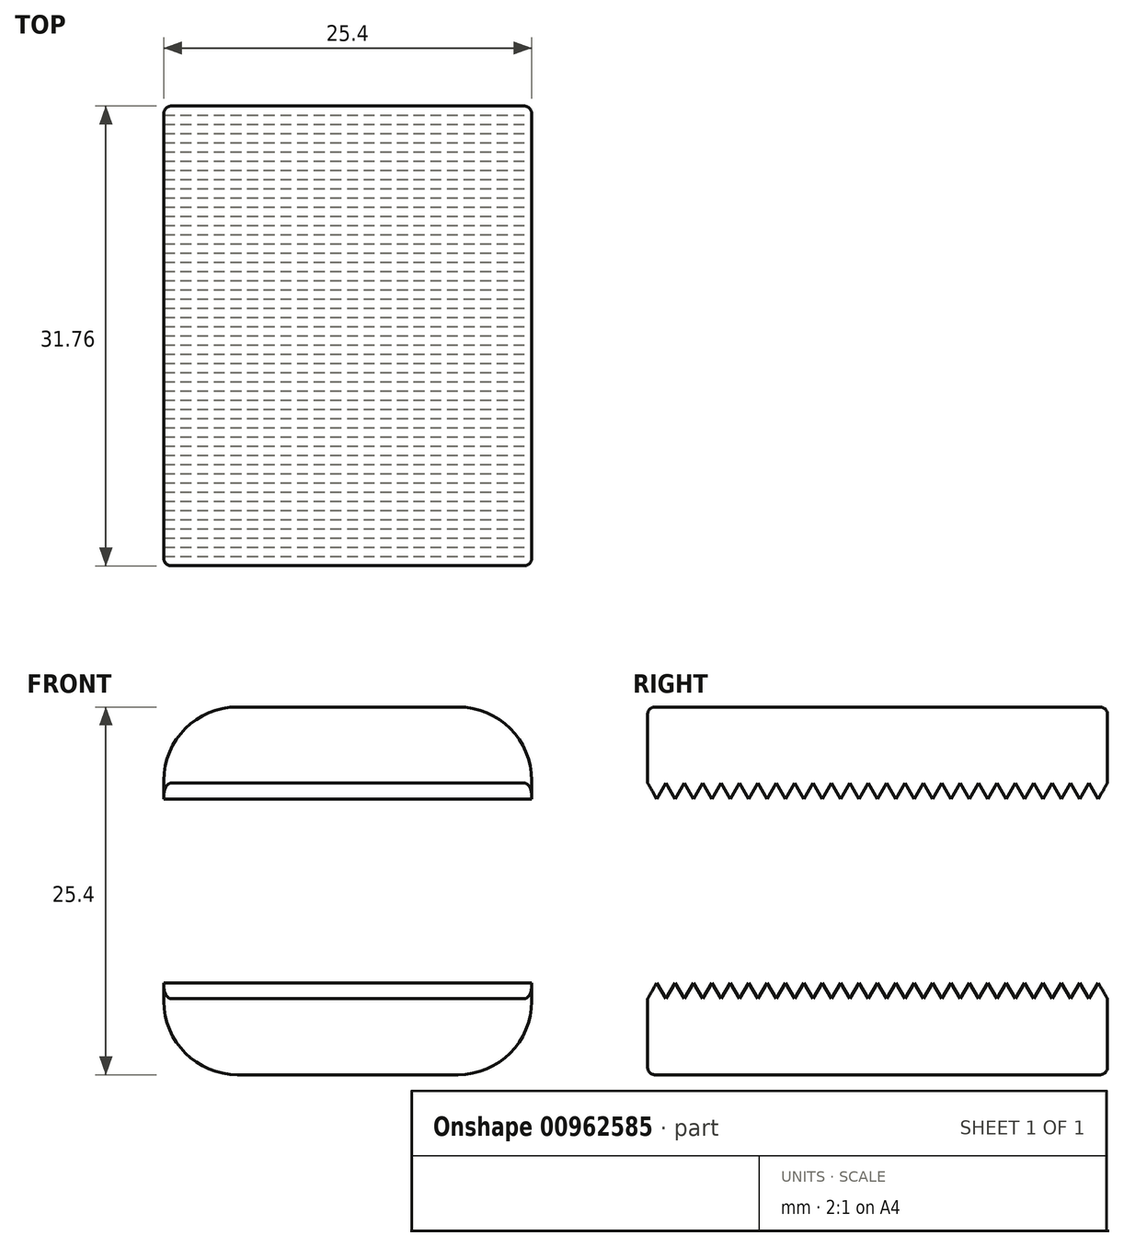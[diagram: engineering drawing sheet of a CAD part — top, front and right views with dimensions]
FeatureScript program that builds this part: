
annotation { "Feature Type Name" : "Feature", "Feature Type Description" : "" }
export const myFeature = defineFeature(function(context is Context, id is Id, definition is map)
    precondition{}
    {
        {
            var Q0;
            Q0=qCreatedBy(makeId("Front.planeOp"),FACE);
            var sketch = newSketch(context, id + "F0", { "sketchPlane" : qUnion([Q0])});
            skLineSegment(sketch, "E0.bottom", {"start": v(12.7, -12.7) * mm, "end": v(-12.7, -12.7) * mm});
            skLineSegment(sketch, "E0.top", {"start": v(12.7, 12.7) * mm, "end": v(-12.7, 12.7) * mm});
            skLineSegment(sketch, "E0.left", {"start": v(12.7, -12.7) * mm, "end": v(12.7, -6.35) * mm});
            skLineSegment(sketch, "E0.right", {"start": v(-12.7, -12.7) * mm, "end": v(-12.7, -6.35) * mm});
            skPoint(sketch, "E0.middle", {"position": v(0, 0) * mm});
            skLineSegment(sketch, "E1.bottom", {"start": v(12.7, -6.35) * mm, "end": v(-12.7, -6.35) * mm});
            skLineSegment(sketch, "E1.top", {"start": v(12.7, 6.35) * mm, "end": v(-12.7, 6.35) * mm});
            skLineSegment(sketch, "E2.trimOffspring", {"start": v(-12.7, 6.35) * mm, "end": v(-12.7, 12.7) * mm});
            skLineSegment(sketch, "E3.trimOffspring", {"start": v(12.7, 6.35) * mm, "end": v(12.7, 12.7) * mm});
            skSolve(sketch);
        }
        {
            var Q0;
            Q0=qSketchRegion(id+"F0",true);
            extrude(context, id + "F1", {"entities" : qUnion([Q0]), "endBound" : BoundingType.SYMMETRIC, "depth" : 31.75 * mm, "offsetDistance" : 25.4 * mm});
        }
        {
            var Q0;
            Q0=qCreatedBy(makeId("Right.planeOp"),FACE);
            var sketch = newSketch(context, id + "F2", { "sketchPlane" : qUnion([Q0])});
            skLineSegment(sketch, "E4", {"start": v(0, 6.35) * mm, "end": v(-0.64, 7.45) * mm});
            skLineSegment(sketch, "E5", {"start": v(-0.63, 7.45) * mm, "end": v(-1.27, 6.35) * mm});
            skLineSegment(sketch, "E6.1.0.0", {"start": v(-1.27, 6.35) * mm, "end": v(-1.9, 7.45) * mm});
            skLineSegment(sketch, "E6.1.0.1", {"start": v(-1.9, 7.45) * mm, "end": v(-2.54, 6.35) * mm});
            skLineSegment(sketch, "E6.2.0.0", {"start": v(-2.54, 6.35) * mm, "end": v(-3.18, 7.45) * mm});
            skLineSegment(sketch, "E6.2.0.1", {"start": v(-3.18, 7.45) * mm, "end": v(-3.81, 6.35) * mm});
            skLineSegment(sketch, "E6.3.0.0", {"start": v(-3.81, 6.35) * mm, "end": v(-4.45, 7.45) * mm});
            skLineSegment(sketch, "E6.3.0.1", {"start": v(-4.45, 7.45) * mm, "end": v(-5.08, 6.35) * mm});
            skLineSegment(sketch, "E6.4.0.0", {"start": v(-5.08, 6.35) * mm, "end": v(-5.72, 7.45) * mm});
            skLineSegment(sketch, "E6.4.0.1", {"start": v(-5.72, 7.45) * mm, "end": v(-6.35, 6.35) * mm});
            skLineSegment(sketch, "E6.5.0.0", {"start": v(-6.35, 6.35) * mm, "end": v(-6.99, 7.45) * mm});
            skLineSegment(sketch, "E6.5.0.1", {"start": v(-6.99, 7.45) * mm, "end": v(-7.62, 6.35) * mm});
            skLineSegment(sketch, "E6.6.0.0", {"start": v(-7.62, 6.35) * mm, "end": v(-8.26, 7.45) * mm});
            skLineSegment(sketch, "E6.6.0.1", {"start": v(-8.26, 7.45) * mm, "end": v(-8.9, 6.35) * mm});
            skLineSegment(sketch, "E6.7.0.0", {"start": v(-8.9, 6.35) * mm, "end": v(-9.53, 7.45) * mm});
            skLineSegment(sketch, "E6.7.0.1", {"start": v(-9.53, 7.45) * mm, "end": v(-10.16, 6.35) * mm});
            skLineSegment(sketch, "E6.8.0.0", {"start": v(-10.16, 6.35) * mm, "end": v(-10.8, 7.45) * mm});
            skLineSegment(sketch, "E6.8.0.1", {"start": v(-10.8, 7.45) * mm, "end": v(-11.43, 6.35) * mm});
            skLineSegment(sketch, "E6.9.0.0", {"start": v(-11.43, 6.35) * mm, "end": v(-12.07, 7.45) * mm});
            skLineSegment(sketch, "E6.9.0.1", {"start": v(-12.07, 7.45) * mm, "end": v(-12.7, 6.35) * mm});
            skLineSegment(sketch, "E6.10.0.0", {"start": v(-12.7, 6.35) * mm, "end": v(-13.34, 7.45) * mm});
            skLineSegment(sketch, "E6.10.0.1", {"start": v(-13.34, 7.45) * mm, "end": v(-13.97, 6.35) * mm});
            skLineSegment(sketch, "E6.11.0.0", {"start": v(-13.97, 6.35) * mm, "end": v(-14.6, 7.45) * mm});
            skLineSegment(sketch, "E6.11.0.1", {"start": v(-14.6, 7.45) * mm, "end": v(-15.24, 6.35) * mm});
            skLineSegment(sketch, "E6.12.0.0", {"start": v(-15.24, 6.35) * mm, "end": v(-15.88, 7.45) * mm});
            skLineSegment(sketch, "E6.12.0.1", {"start": v(-15.88, 7.45) * mm, "end": v(-16.51, 6.35) * mm});
            skLineSegment(sketch, "E6.13.0.0", {"start": v(-16.51, 6.35) * mm, "end": v(-17.15, 7.45) * mm});
            skLineSegment(sketch, "E6.13.0.1", {"start": v(-17.14, 7.45) * mm, "end": v(-17.78, 6.35) * mm});
            skLineSegment(sketch, "E6.14.0.0", {"start": v(-17.78, 6.35) * mm, "end": v(-18.41, 7.45) * mm});
            skLineSegment(sketch, "E6.14.0.1", {"start": v(-18.42, 7.45) * mm, "end": v(-19.05, 6.35) * mm});
            skLineSegment(sketch, "E6.15.0.0", {"start": v(-19.05, 6.35) * mm, "end": v(-19.69, 7.45) * mm});
            skLineSegment(sketch, "E6.15.0.1", {"start": v(-19.69, 7.45) * mm, "end": v(-20.32, 6.35) * mm});
            skLineSegment(sketch, "E6.16.0.0", {"start": v(-20.32, 6.35) * mm, "end": v(-20.96, 7.45) * mm});
            skLineSegment(sketch, "E6.16.0.1", {"start": v(-20.96, 7.45) * mm, "end": v(-21.6, 6.35) * mm});
            skLineSegment(sketch, "E6.17.0.0", {"start": v(-21.6, 6.35) * mm, "end": v(-22.23, 7.45) * mm});
            skLineSegment(sketch, "E6.17.0.1", {"start": v(-22.23, 7.45) * mm, "end": v(-22.86, 6.35) * mm});
            skLineSegment(sketch, "E6.18.0.0", {"start": v(-22.86, 6.35) * mm, "end": v(-23.5, 7.45) * mm});
            skLineSegment(sketch, "E6.18.0.1", {"start": v(-23.5, 7.45) * mm, "end": v(-24.13, 6.35) * mm});
            skLineSegment(sketch, "E6.19.0.0", {"start": v(-24.13, 6.35) * mm, "end": v(-24.77, 7.45) * mm});
            skLineSegment(sketch, "E6.19.0.1", {"start": v(-24.77, 7.45) * mm, "end": v(-25.4, 6.35) * mm});
            skLineSegment(sketch, "E6.20.0.0", {"start": v(-25.4, 6.35) * mm, "end": v(-26.04, 7.45) * mm});
            skLineSegment(sketch, "E6.20.0.1", {"start": v(-26.04, 7.45) * mm, "end": v(-26.67, 6.35) * mm});
            skLineSegment(sketch, "E6.21.0.0", {"start": v(-26.67, 6.35) * mm, "end": v(-27.3, 7.45) * mm});
            skLineSegment(sketch, "E6.21.0.1", {"start": v(-27.3, 7.45) * mm, "end": v(-27.94, 6.35) * mm});
            skLineSegment(sketch, "E6.22.0.0", {"start": v(-27.94, 6.35) * mm, "end": v(-28.58, 7.45) * mm});
            skLineSegment(sketch, "E6.22.0.1", {"start": v(-28.58, 7.45) * mm, "end": v(-29.21, 6.35) * mm});
            skLineSegment(sketch, "E6.23.0.0", {"start": v(-29.21, 6.35) * mm, "end": v(-29.85, 7.45) * mm});
            skLineSegment(sketch, "E6.23.0.1", {"start": v(-29.85, 7.45) * mm, "end": v(-30.48, 6.35) * mm});
            skLineSegment(sketch, "E6.direction1", {"start": v(-1.27, 6.35) * mm, "end": v(-2.54, 6.35) * mm, "construction": true});
            skLineSegment(sketch, "E7.1.0.0", {"start": v(0.64, 7.45) * mm, "end": v(0, 6.35) * mm});
            skLineSegment(sketch, "E7.1.0.1", {"start": v(1.27, 6.35) * mm, "end": v(0.64, 7.45) * mm});
            skLineSegment(sketch, "E7.2.0.0", {"start": v(1.9, 7.45) * mm, "end": v(1.27, 6.35) * mm});
            skLineSegment(sketch, "E7.2.0.1", {"start": v(2.54, 6.35) * mm, "end": v(1.9, 7.45) * mm});
            skLineSegment(sketch, "E7.3.0.0", {"start": v(3.18, 7.45) * mm, "end": v(2.54, 6.35) * mm});
            skLineSegment(sketch, "E7.3.0.1", {"start": v(3.81, 6.35) * mm, "end": v(3.18, 7.45) * mm});
            skLineSegment(sketch, "E7.4.0.0", {"start": v(4.45, 7.45) * mm, "end": v(3.81, 6.35) * mm});
            skLineSegment(sketch, "E7.4.0.1", {"start": v(5.08, 6.35) * mm, "end": v(4.45, 7.45) * mm});
            skLineSegment(sketch, "E7.5.0.0", {"start": v(5.72, 7.45) * mm, "end": v(5.08, 6.35) * mm});
            skLineSegment(sketch, "E7.5.0.1", {"start": v(6.35, 6.35) * mm, "end": v(5.72, 7.45) * mm});
            skLineSegment(sketch, "E7.6.0.0", {"start": v(6.99, 7.45) * mm, "end": v(6.35, 6.35) * mm});
            skLineSegment(sketch, "E7.6.0.1", {"start": v(7.62, 6.35) * mm, "end": v(6.99, 7.45) * mm});
            skLineSegment(sketch, "E7.7.0.0", {"start": v(8.26, 7.45) * mm, "end": v(7.62, 6.35) * mm});
            skLineSegment(sketch, "E7.7.0.1", {"start": v(8.9, 6.35) * mm, "end": v(8.26, 7.45) * mm});
            skLineSegment(sketch, "E7.8.0.0", {"start": v(9.53, 7.45) * mm, "end": v(8.9, 6.35) * mm});
            skLineSegment(sketch, "E7.8.0.1", {"start": v(10.16, 6.35) * mm, "end": v(9.53, 7.45) * mm});
            skLineSegment(sketch, "E7.9.0.0", {"start": v(10.8, 7.45) * mm, "end": v(10.16, 6.35) * mm});
            skLineSegment(sketch, "E7.9.0.1", {"start": v(11.43, 6.35) * mm, "end": v(10.8, 7.45) * mm});
            skLineSegment(sketch, "E7.10.0.0", {"start": v(12.07, 7.45) * mm, "end": v(11.43, 6.35) * mm});
            skLineSegment(sketch, "E7.10.0.1", {"start": v(12.7, 6.35) * mm, "end": v(12.07, 7.45) * mm});
            skLineSegment(sketch, "E7.11.0.0", {"start": v(13.34, 7.45) * mm, "end": v(12.7, 6.35) * mm});
            skLineSegment(sketch, "E7.11.0.1", {"start": v(13.97, 6.35) * mm, "end": v(13.34, 7.45) * mm});
            skLineSegment(sketch, "E7.12.0.0", {"start": v(14.6, 7.45) * mm, "end": v(13.97, 6.35) * mm});
            skLineSegment(sketch, "E7.12.0.1", {"start": v(15.24, 6.35) * mm, "end": v(14.6, 7.45) * mm});
            skLineSegment(sketch, "E7.13.0.0", {"start": v(15.88, 7.45) * mm, "end": v(15.24, 6.35) * mm});
            skLineSegment(sketch, "E7.13.0.1", {"start": v(16.51, 6.35) * mm, "end": v(15.88, 7.45) * mm});
            skLineSegment(sketch, "E7.14.0.0", {"start": v(17.15, 7.45) * mm, "end": v(16.51, 6.35) * mm});
            skLineSegment(sketch, "E7.14.0.1", {"start": v(17.78, 6.35) * mm, "end": v(17.15, 7.45) * mm});
            skLineSegment(sketch, "E7.15.0.0", {"start": v(18.42, 7.45) * mm, "end": v(17.78, 6.35) * mm});
            skLineSegment(sketch, "E7.15.0.1", {"start": v(19.05, 6.35) * mm, "end": v(18.42, 7.45) * mm});
            skLineSegment(sketch, "E7.16.0.0", {"start": v(19.69, 7.45) * mm, "end": v(19.05, 6.35) * mm});
            skLineSegment(sketch, "E7.16.0.1", {"start": v(20.32, 6.35) * mm, "end": v(19.69, 7.45) * mm});
            skLineSegment(sketch, "E7.17.0.0", {"start": v(20.96, 7.45) * mm, "end": v(20.32, 6.35) * mm});
            skLineSegment(sketch, "E7.17.0.1", {"start": v(21.6, 6.35) * mm, "end": v(20.96, 7.45) * mm});
            skLineSegment(sketch, "E7.18.0.0", {"start": v(22.23, 7.45) * mm, "end": v(21.6, 6.35) * mm});
            skLineSegment(sketch, "E7.18.0.1", {"start": v(22.86, 6.35) * mm, "end": v(22.23, 7.45) * mm});
            skLineSegment(sketch, "E7.19.0.0", {"start": v(23.5, 7.45) * mm, "end": v(22.86, 6.35) * mm});
            skLineSegment(sketch, "E7.19.0.1", {"start": v(24.13, 6.35) * mm, "end": v(23.5, 7.45) * mm});
            skLineSegment(sketch, "E7.20.0.0", {"start": v(24.77, 7.45) * mm, "end": v(24.13, 6.35) * mm});
            skLineSegment(sketch, "E7.20.0.1", {"start": v(25.4, 6.35) * mm, "end": v(24.77, 7.45) * mm});
            skLineSegment(sketch, "E7.21.0.0", {"start": v(26.04, 7.45) * mm, "end": v(25.4, 6.35) * mm});
            skLineSegment(sketch, "E7.21.0.1", {"start": v(26.67, 6.35) * mm, "end": v(26.04, 7.45) * mm});
            skLineSegment(sketch, "E7.22.0.0", {"start": v(27.3, 7.45) * mm, "end": v(26.67, 6.35) * mm});
            skLineSegment(sketch, "E7.22.0.1", {"start": v(27.94, 6.35) * mm, "end": v(27.3, 7.45) * mm});
            skLineSegment(sketch, "E7.23.0.0", {"start": v(28.58, 7.45) * mm, "end": v(27.94, 6.35) * mm});
            skLineSegment(sketch, "E7.23.0.1", {"start": v(29.21, 6.35) * mm, "end": v(28.58, 7.45) * mm});
            skLineSegment(sketch, "E7.24.0.0", {"start": v(29.85, 7.45) * mm, "end": v(29.21, 6.35) * mm});
            skLineSegment(sketch, "E7.24.0.1", {"start": v(30.48, 6.35) * mm, "end": v(29.85, 7.45) * mm});
            skLineSegment(sketch, "E7.direction1", {"start": v(-1.27, 6.35) * mm, "end": v(0, 6.35) * mm, "construction": true});
            skLineSegment(sketch, "E8", {"start": v(-65.02, 6.35) * mm, "end": v(-65.02, 6.1) * mm});
            skLineSegment(sketch, "E9", {"start": v(-65.02, 6.35) * mm, "end": v(65.02, 6.35) * mm});
            skLineSegment(sketch, "E10", {"start": v(65.02, 6.35) * mm, "end": v(65.02, 6.6) * mm});
            skLineSegment(sketch, "E11.MirrorCS", {"start": v(39.12, -7.23) * mm, "end": v(38.6, -6.35) * mm});
            skLineSegment(sketch, "E12.MirrorCS", {"start": v(0, -6.35) * mm, "end": v(-0.63, -7.45) * mm});
            skLineSegment(sketch, "E13.MirrorCS", {"start": v(6.99, -7.45) * mm, "end": v(6.35, -6.35) * mm});
            skLineSegment(sketch, "E14.MirrorCS", {"start": v(38.1, -7.23) * mm, "end": v(37.6, -6.35) * mm});
            skLineSegment(sketch, "E15.MirrorCS", {"start": v(-57.4, -7.23) * mm, "end": v(-57.91, -6.35) * mm});
            skLineSegment(sketch, "E16.MirrorCS", {"start": v(-2.54, -6.35) * mm, "end": v(-3.18, -7.45) * mm});
            skLineSegment(sketch, "E17.MirrorCS", {"start": v(2.54, -6.35) * mm, "end": v(1.9, -7.45) * mm});
            skLineSegment(sketch, "E18.MirrorCS", {"start": v(8.26, -7.45) * mm, "end": v(7.62, -6.35) * mm});
            skLineSegment(sketch, "E19.MirrorCS", {"start": v(-56.39, -7.23) * mm, "end": v(-56.9, -6.35) * mm});
            skLineSegment(sketch, "E20.MirrorCS", {"start": v(12.7, -6.35) * mm, "end": v(12.07, -7.45) * mm});
            skLineSegment(sketch, "E21.MirrorCS", {"start": v(6.35, -6.35) * mm, "end": v(5.72, -7.45) * mm});
            skLineSegment(sketch, "E22.MirrorCS", {"start": v(-30.48, -6.35) * mm, "end": v(-31.12, -7.45) * mm});
            skLineSegment(sketch, "E23.MirrorCS", {"start": v(40.64, -6.35) * mm, "end": v(40.13, -7.23) * mm});
            skLineSegment(sketch, "E24.MirrorCS", {"start": v(-1.27, -6.35) * mm, "end": v(0, -6.35) * mm, "construction": true});
            skLineSegment(sketch, "E25.MirrorCS", {"start": v(-1.27, -6.35) * mm, "end": v(-2.54, -6.35) * mm, "construction": true});
            skLineSegment(sketch, "E26.MirrorCS", {"start": v(-34.04, -7.23) * mm, "end": v(-34.54, -6.35) * mm});
            skLineSegment(sketch, "E27.MirrorCS", {"start": v(13.97, -6.35) * mm, "end": v(13.34, -7.45) * mm});
            skLineSegment(sketch, "E28.MirrorCS", {"start": v(1.9, -7.45) * mm, "end": v(1.27, -6.35) * mm});
            skLineSegment(sketch, "E29.MirrorCS", {"start": v(5.72, -7.45) * mm, "end": v(5.08, -6.35) * mm});
            skLineSegment(sketch, "E30.MirrorCS", {"start": v(-10.16, -6.35) * mm, "end": v(-10.8, -7.45) * mm});
            skLineSegment(sketch, "E31.MirrorCS", {"start": v(11.43, -6.35) * mm, "end": v(10.8, -7.45) * mm});
            skLineSegment(sketch, "E32.MirrorCS", {"start": v(-55.88, -6.35) * mm, "end": v(-56.39, -7.23) * mm});
            skLineSegment(sketch, "E33.MirrorCS", {"start": v(-1.27, -6.35) * mm, "end": v(-1.9, -7.45) * mm});
            skLineSegment(sketch, "E34.MirrorCS", {"start": v(53.85, -6.35) * mm, "end": v(53.34, -7.23) * mm});
            skLineSegment(sketch, "E35.MirrorCS", {"start": v(7.62, -6.35) * mm, "end": v(6.99, -7.45) * mm});
            skLineSegment(sketch, "E36.MirrorCS", {"start": v(-1.9, -7.45) * mm, "end": v(-2.54, -6.35) * mm});
            skLineSegment(sketch, "E37.MirrorCS", {"start": v(-49.28, -7.23) * mm, "end": v(-49.78, -6.35) * mm});
            skLineSegment(sketch, "E38.MirrorCS", {"start": v(22.86, -6.35) * mm, "end": v(22.23, -7.45) * mm});
            skLineSegment(sketch, "E39.MirrorCS", {"start": v(-48.26, -7.23) * mm, "end": v(-48.77, -6.35) * mm});
            skLineSegment(sketch, "E40.MirrorCS", {"start": v(34.54, -6.35) * mm, "end": v(34.04, -7.23) * mm});
            skLineSegment(sketch, "E41.MirrorCS", {"start": v(-28.58, -7.45) * mm, "end": v(-29.21, -6.35) * mm});
            skLineSegment(sketch, "E42.MirrorCS", {"start": v(4.45, -7.45) * mm, "end": v(3.81, -6.35) * mm});
            skLineSegment(sketch, "E43.MirrorCS", {"start": v(-22.86, -6.35) * mm, "end": v(-23.5, -7.45) * mm});
            skLineSegment(sketch, "E44.MirrorCS", {"start": v(-32.39, -7.45) * mm, "end": v(-33.02, -6.35) * mm});
            skLineSegment(sketch, "E45.MirrorCS", {"start": v(28.58, -7.45) * mm, "end": v(27.94, -6.35) * mm});
            skLineSegment(sketch, "E46.MirrorCS", {"start": v(63, -6.35) * mm, "end": v(62.48, -7.23) * mm});
            skLineSegment(sketch, "E47.MirrorCS", {"start": v(30.99, -7.23) * mm, "end": v(30.48, -6.35) * mm});
            skLineSegment(sketch, "E48.MirrorCS", {"start": v(14.6, -7.45) * mm, "end": v(13.97, -6.35) * mm});
            skLineSegment(sketch, "E49.MirrorCS", {"start": v(1.27, -6.35) * mm, "end": v(0.64, -7.45) * mm});
            skLineSegment(sketch, "E50.MirrorCS", {"start": v(-30.48, -6.35) * mm, "end": v(-30.99, -7.23) * mm});
            skLineSegment(sketch, "E51.MirrorCS", {"start": v(38.6, -6.35) * mm, "end": v(38.1, -7.23) * mm});
            skLineSegment(sketch, "E52.MirrorCS", {"start": v(29.97, -7.23) * mm, "end": v(29.46, -6.35) * mm});
            skLineSegment(sketch, "E53.MirrorCS", {"start": v(12.07, -7.45) * mm, "end": v(11.43, -6.35) * mm});
            skLineSegment(sketch, "E54.MirrorCS", {"start": v(-55.37, -7.23) * mm, "end": v(-55.88, -6.35) * mm});
            skLineSegment(sketch, "E55.MirrorCS", {"start": v(3.18, -7.45) * mm, "end": v(2.54, -6.35) * mm});
            skLineSegment(sketch, "E56.MirrorCS", {"start": v(-20.32, -6.35) * mm, "end": v(-20.96, -7.45) * mm});
            skLineSegment(sketch, "E57.MirrorCS", {"start": v(54.86, -6.35) * mm, "end": v(54.36, -7.23) * mm});
            skLineSegment(sketch, "E58.MirrorCS", {"start": v(13.34, -7.45) * mm, "end": v(12.7, -6.35) * mm});
            skLineSegment(sketch, "E59.MirrorCS", {"start": v(39.62, -6.35) * mm, "end": v(39.12, -7.23) * mm});
            skLineSegment(sketch, "E60.MirrorCS", {"start": v(-29.46, -6.35) * mm, "end": v(-29.97, -7.23) * mm});
            skLineSegment(sketch, "E61.MirrorCS", {"start": v(-56.9, -6.35) * mm, "end": v(-57.4, -7.23) * mm});
            skLineSegment(sketch, "E62.MirrorCS", {"start": v(-18.42, -7.45) * mm, "end": v(-19.05, -6.35) * mm});
            skLineSegment(sketch, "E63.MirrorCS", {"start": v(-12.7, -6.35) * mm, "end": v(-13.34, -7.45) * mm});
            skLineSegment(sketch, "E64.MirrorCS", {"start": v(50.3, -7.23) * mm, "end": v(49.78, -6.35) * mm});
            skLineSegment(sketch, "E65.MirrorCS", {"start": v(-44.7, -6.35) * mm, "end": v(-45.21, -7.23) * mm});
            skLineSegment(sketch, "E66.MirrorCS", {"start": v(61.98, -6.35) * mm, "end": v(61.47, -7.23) * mm});
            skLineSegment(sketch, "E67.MirrorCS", {"start": v(17.15, -7.45) * mm, "end": v(16.51, -6.35) * mm});
            skLineSegment(sketch, "E68.MirrorCS", {"start": v(-3.18, -7.45) * mm, "end": v(-3.81, -6.35) * mm});
            skLineSegment(sketch, "E69.MirrorCS", {"start": v(-57.91, -6.35) * mm, "end": v(-58.42, -7.23) * mm});
            skLineSegment(sketch, "E70.MirrorCS", {"start": v(-41.15, -7.23) * mm, "end": v(-41.66, -6.35) * mm});
            skLineSegment(sketch, "E71.MirrorCS", {"start": v(18.42, -7.45) * mm, "end": v(17.78, -6.35) * mm});
            skLineSegment(sketch, "E72.MirrorCS", {"start": v(-17.14, -7.45) * mm, "end": v(-17.78, -6.35) * mm});
            skLineSegment(sketch, "E73.MirrorCS", {"start": v(-37.6, -6.35) * mm, "end": v(-38.1, -7.23) * mm});
            skLineSegment(sketch, "E74.MirrorCS", {"start": v(3.81, -6.35) * mm, "end": v(3.18, -7.45) * mm});
            skLineSegment(sketch, "E75.MirrorCS", {"start": v(27.3, -7.45) * mm, "end": v(26.67, -6.35) * mm});
            skLineSegment(sketch, "E76.MirrorCS", {"start": v(40.13, -7.23) * mm, "end": v(39.62, -6.35) * mm});
            skLineSegment(sketch, "E77.MirrorCS", {"start": v(42.16, -7.23) * mm, "end": v(41.66, -6.35) * mm});
            skLineSegment(sketch, "E78.MirrorCS", {"start": v(0.64, -7.45) * mm, "end": v(0, -6.35) * mm});
            skLineSegment(sketch, "E79.MirrorCS", {"start": v(-58.93, -6.35) * mm, "end": v(-59.44, -7.23) * mm});
            skLineSegment(sketch, "E80.MirrorCS", {"start": v(-38.6, -6.35) * mm, "end": v(-39.12, -7.23) * mm});
            skLineSegment(sketch, "E81.MirrorCS", {"start": v(45.72, -6.35) * mm, "end": v(45.21, -7.23) * mm});
            skLineSegment(sketch, "E82.MirrorCS", {"start": v(46.74, -6.35) * mm, "end": v(46.23, -7.23) * mm});
            skLineSegment(sketch, "E83.MirrorCS", {"start": v(-60.96, -6.35) * mm, "end": v(-61.47, -7.23) * mm});
            skLineSegment(sketch, "E84.MirrorCS", {"start": v(-0.63, -7.45) * mm, "end": v(-1.27, -6.35) * mm});
            skLineSegment(sketch, "E85.MirrorCS", {"start": v(37.6, -6.35) * mm, "end": v(37.08, -7.23) * mm});
            skLineSegment(sketch, "E86.MirrorCS", {"start": v(58.42, -7.23) * mm, "end": v(57.91, -6.35) * mm});
            skLineSegment(sketch, "E87.MirrorCS", {"start": v(15.24, -6.35) * mm, "end": v(14.6, -7.45) * mm});
            skLineSegment(sketch, "E88.MirrorCS", {"start": v(-52.83, -6.35) * mm, "end": v(-53.34, -7.23) * mm});
            skLineSegment(sketch, "E89.MirrorCS", {"start": v(5.08, -6.35) * mm, "end": v(4.45, -7.45) * mm});
            skLineSegment(sketch, "E90.MirrorCS", {"start": v(33.02, -6.35) * mm, "end": v(32.39, -7.45) * mm});
            skLineSegment(sketch, "E91.MirrorCS", {"start": v(8.9, -6.35) * mm, "end": v(8.26, -7.45) * mm});
            skLineSegment(sketch, "E92.MirrorCS", {"start": v(-27.3, -7.45) * mm, "end": v(-27.94, -6.35) * mm});
            skLineSegment(sketch, "E93.MirrorCS", {"start": v(16.51, -6.35) * mm, "end": v(15.88, -7.45) * mm});
            skLineSegment(sketch, "E94.MirrorCS", {"start": v(-47.75, -6.35) * mm, "end": v(-48.26, -7.23) * mm});
            skLineSegment(sketch, "E95.MirrorCS", {"start": v(-51.82, -6.35) * mm, "end": v(-52.32, -7.23) * mm});
            skLineSegment(sketch, "E96.MirrorCS", {"start": v(54.36, -7.23) * mm, "end": v(53.85, -6.35) * mm});
            skLineSegment(sketch, "E97.MirrorCS", {"start": v(9.53, -7.45) * mm, "end": v(8.9, -6.35) * mm});
            skLineSegment(sketch, "E98.MirrorCS", {"start": v(-23.5, -7.45) * mm, "end": v(-24.13, -6.35) * mm});
            skLineSegment(sketch, "E99.MirrorCS", {"start": v(-17.78, -6.35) * mm, "end": v(-18.41, -7.45) * mm});
            skLineSegment(sketch, "E100.MirrorCS", {"start": v(-22.23, -7.45) * mm, "end": v(-22.86, -6.35) * mm});
            skLineSegment(sketch, "E101.MirrorCS", {"start": v(52.83, -6.35) * mm, "end": v(52.32, -7.23) * mm});
            skLineSegment(sketch, "E102.MirrorCS", {"start": v(42.67, -6.35) * mm, "end": v(42.16, -7.23) * mm});
            skLineSegment(sketch, "E103.MirrorCS", {"start": v(-30.99, -7.23) * mm, "end": v(-31.5, -6.35) * mm});
            skLineSegment(sketch, "E104.MirrorCS", {"start": v(-34.92, -7.45) * mm, "end": v(-35.56, -6.35) * mm});
            skLineSegment(sketch, "E105.MirrorCS", {"start": v(-52.32, -7.23) * mm, "end": v(-52.83, -6.35) * mm});
            skLineSegment(sketch, "E106.MirrorCS", {"start": v(43.69, -6.35) * mm, "end": v(43.18, -7.23) * mm});
            skLineSegment(sketch, "E107.MirrorCS", {"start": v(52.32, -7.23) * mm, "end": v(51.82, -6.35) * mm});
            skLineSegment(sketch, "E108.MirrorCS", {"start": v(30.48, -6.35) * mm, "end": v(29.97, -7.23) * mm});
            skLineSegment(sketch, "E109.MirrorCS", {"start": v(-35.56, -6.35) * mm, "end": v(-36.07, -7.23) * mm});
            skLineSegment(sketch, "E110.MirrorCS", {"start": v(36.83, -6.35) * mm, "end": v(36.2, -7.45) * mm});
            skLineSegment(sketch, "E111.MirrorCS", {"start": v(10.16, -6.35) * mm, "end": v(9.53, -7.45) * mm});
            skLineSegment(sketch, "E112.MirrorCS", {"start": v(-60.45, -7.23) * mm, "end": v(-60.96, -6.35) * mm});
            skLineSegment(sketch, "E113.MirrorCS", {"start": v(36.58, -6.35) * mm, "end": v(36.07, -7.23) * mm});
            skLineSegment(sketch, "E114.MirrorCS", {"start": v(-40.64, -6.35) * mm, "end": v(-41.15, -7.23) * mm});
            skLineSegment(sketch, "E115.MirrorCS", {"start": v(15.88, -7.45) * mm, "end": v(15.24, -6.35) * mm});
            skLineSegment(sketch, "E116.MirrorCS", {"start": v(-10.8, -7.45) * mm, "end": v(-11.43, -6.35) * mm});
            skLineSegment(sketch, "E117.MirrorCS", {"start": v(-54.36, -7.23) * mm, "end": v(-54.86, -6.35) * mm});
            skLineSegment(sketch, "E118.MirrorCS", {"start": v(62.48, -7.23) * mm, "end": v(61.98, -6.35) * mm});
            skLineSegment(sketch, "E119.MirrorCS", {"start": v(-62.48, -7.23) * mm, "end": v(-63, -6.35) * mm});
            skLineSegment(sketch, "E120.MirrorCS", {"start": v(-26.67, -6.35) * mm, "end": v(-27.3, -7.45) * mm});
            skLineSegment(sketch, "E121.MirrorCS", {"start": v(32.39, -7.45) * mm, "end": v(31.75, -6.35) * mm});
            skLineSegment(sketch, "E122.MirrorCS", {"start": v(-8.26, -7.45) * mm, "end": v(-8.9, -6.35) * mm});
            skLineSegment(sketch, "E123.MirrorCS", {"start": v(-44.2, -7.23) * mm, "end": v(-44.7, -6.35) * mm});
            skLineSegment(sketch, "E124.MirrorCS", {"start": v(-29.97, -7.23) * mm, "end": v(-30.48, -6.35) * mm});
            skLineSegment(sketch, "E125.MirrorCS", {"start": v(44.7, -6.35) * mm, "end": v(44.2, -7.23) * mm});
            skLineSegment(sketch, "E126.MirrorCS", {"start": v(-12.07, -7.45) * mm, "end": v(-12.7, -6.35) * mm});
            skLineSegment(sketch, "E127.MirrorCS", {"start": v(-45.72, -6.35) * mm, "end": v(-46.23, -7.23) * mm});
            skLineSegment(sketch, "E128.MirrorCS", {"start": v(37.08, -7.23) * mm, "end": v(36.58, -6.35) * mm});
            skLineSegment(sketch, "E129.MirrorCS", {"start": v(22.23, -7.45) * mm, "end": v(21.6, -6.35) * mm});
            skLineSegment(sketch, "E130.MirrorCS", {"start": v(21.6, -6.35) * mm, "end": v(20.96, -7.45) * mm});
            skLineSegment(sketch, "E131.MirrorCS", {"start": v(23.5, -7.45) * mm, "end": v(22.86, -6.35) * mm});
            skLineSegment(sketch, "E132.MirrorCS", {"start": v(60.96, -6.35) * mm, "end": v(60.45, -7.23) * mm});
            skLineSegment(sketch, "E133.MirrorCS", {"start": v(17.78, -6.35) * mm, "end": v(17.15, -7.45) * mm});
            skLineSegment(sketch, "E134.MirrorCS", {"start": v(-4.45, -7.45) * mm, "end": v(-5.08, -6.35) * mm});
            skLineSegment(sketch, "E135.MirrorCS", {"start": v(57.91, -6.35) * mm, "end": v(57.4, -7.23) * mm});
            skLineSegment(sketch, "E136.MirrorCS", {"start": v(-16.51, -6.35) * mm, "end": v(-17.15, -7.45) * mm});
            skLineSegment(sketch, "E137.MirrorCS", {"start": v(31.12, -7.45) * mm, "end": v(30.48, -6.35) * mm});
            skLineSegment(sketch, "E138.MirrorCS", {"start": v(-15.24, -6.35) * mm, "end": v(-15.88, -7.45) * mm});
            skLineSegment(sketch, "E139.MirrorCS", {"start": v(-36.2, -7.45) * mm, "end": v(-36.83, -6.35) * mm});
            skLineSegment(sketch, "E140.MirrorCS", {"start": v(20.32, -6.35) * mm, "end": v(19.69, -7.45) * mm});
            skLineSegment(sketch, "E141.MirrorCS", {"start": v(-21.6, -6.35) * mm, "end": v(-22.23, -7.45) * mm});
            skLineSegment(sketch, "E142.MirrorCS", {"start": v(-48.77, -6.35) * mm, "end": v(-49.28, -7.23) * mm});
            skLineSegment(sketch, "E143.MirrorCS", {"start": v(-19.05, -6.35) * mm, "end": v(-19.69, -7.45) * mm});
            skLineSegment(sketch, "E144.MirrorCS", {"start": v(-47.24, -7.23) * mm, "end": v(-47.75, -6.35) * mm});
            skLineSegment(sketch, "E145.MirrorCS", {"start": v(-50.8, -6.35) * mm, "end": v(-51.3, -7.23) * mm});
            skLineSegment(sketch, "E146.MirrorCS", {"start": v(60.45, -7.23) * mm, "end": v(59.94, -6.35) * mm});
            skLineSegment(sketch, "E147.MirrorCS", {"start": v(-3.81, -6.35) * mm, "end": v(-4.45, -7.45) * mm});
            skLineSegment(sketch, "E148.MirrorCS", {"start": v(-39.62, -6.35) * mm, "end": v(-40.13, -7.23) * mm});
            skLineSegment(sketch, "E149.MirrorCS", {"start": v(-36.58, -6.35) * mm, "end": v(-37.08, -7.23) * mm});
            skLineSegment(sketch, "E150.MirrorCS", {"start": v(-49.78, -6.35) * mm, "end": v(-50.3, -7.23) * mm});
            skLineSegment(sketch, "E151.MirrorCS", {"start": v(-58.42, -7.23) * mm, "end": v(-58.93, -6.35) * mm});
            skLineSegment(sketch, "E152.MirrorCS", {"start": v(-33.66, -7.45) * mm, "end": v(-34.3, -6.35) * mm});
            skLineSegment(sketch, "E153.MirrorCS", {"start": v(35.56, -6.35) * mm, "end": v(35.05, -7.23) * mm});
            skLineSegment(sketch, "E154.MirrorCS", {"start": v(-59.44, -7.23) * mm, "end": v(-59.94, -6.35) * mm});
            skLineSegment(sketch, "E155.MirrorCS", {"start": v(-20.96, -7.45) * mm, "end": v(-21.6, -6.35) * mm});
            skLineSegment(sketch, "E156.MirrorCS", {"start": v(-34.54, -6.35) * mm, "end": v(-35.05, -7.23) * mm});
            skLineSegment(sketch, "E157.MirrorCS", {"start": v(-31.75, -6.35) * mm, "end": v(-32.39, -7.45) * mm});
            skLineSegment(sketch, "E158.MirrorCS", {"start": v(19.69, -7.45) * mm, "end": v(19.05, -6.35) * mm});
            skLineSegment(sketch, "E159.MirrorCS", {"start": v(-29.85, -7.45) * mm, "end": v(-30.48, -6.35) * mm});
            skLineSegment(sketch, "E160.MirrorCS", {"start": v(-37.08, -7.23) * mm, "end": v(-37.6, -6.35) * mm});
            skLineSegment(sketch, "E161.MirrorCS", {"start": v(34.3, -6.35) * mm, "end": v(33.66, -7.45) * mm});
            skLineSegment(sketch, "E162.MirrorCS", {"start": v(41.66, -6.35) * mm, "end": v(41.15, -7.23) * mm});
            skLineSegment(sketch, "E163.MirrorCS", {"start": v(-40.13, -7.23) * mm, "end": v(-40.64, -6.35) * mm});
            skLineSegment(sketch, "E164.MirrorCS", {"start": v(-29.21, -6.35) * mm, "end": v(-29.85, -7.45) * mm});
            skLineSegment(sketch, "E165.MirrorCS", {"start": v(-13.34, -7.45) * mm, "end": v(-13.97, -6.35) * mm});
            skLineSegment(sketch, "E166.MirrorCS", {"start": v(32, -7.23) * mm, "end": v(31.5, -6.35) * mm});
            skLineSegment(sketch, "E167.MirrorCS", {"start": v(-24.13, -6.35) * mm, "end": v(-24.77, -7.45) * mm});
            skLineSegment(sketch, "E168.MirrorCS", {"start": v(55.37, -7.23) * mm, "end": v(54.86, -6.35) * mm});
            skLineSegment(sketch, "E169.MirrorCS", {"start": v(51.82, -6.35) * mm, "end": v(51.3, -7.23) * mm});
            skLineSegment(sketch, "E170.MirrorCS", {"start": v(34.04, -7.23) * mm, "end": v(33.53, -6.35) * mm});
            skLineSegment(sketch, "E171.MirrorCS", {"start": v(-27.94, -6.35) * mm, "end": v(-28.58, -7.45) * mm});
            skLineSegment(sketch, "E172.MirrorCS", {"start": v(35.56, -6.35) * mm, "end": v(34.93, -7.45) * mm});
            skLineSegment(sketch, "E173.MirrorCS", {"start": v(-45.21, -7.23) * mm, "end": v(-45.72, -6.35) * mm});
            skLineSegment(sketch, "E174.MirrorCS", {"start": v(24.77, -7.45) * mm, "end": v(24.13, -6.35) * mm});
            skLineSegment(sketch, "E175.MirrorCS", {"start": v(31.75, -6.35) * mm, "end": v(31.12, -7.45) * mm});
            skLineSegment(sketch, "E176.MirrorCS", {"start": v(35.05, -7.23) * mm, "end": v(34.54, -6.35) * mm});
            skLineSegment(sketch, "E177.MirrorCS", {"start": v(-38.1, -7.23) * mm, "end": v(-38.6, -6.35) * mm});
            skLineSegment(sketch, "E178.MirrorCS", {"start": v(36.2, -7.45) * mm, "end": v(35.56, -6.35) * mm});
            skLineSegment(sketch, "E179.MirrorCS", {"start": v(-24.77, -7.45) * mm, "end": v(-25.4, -6.35) * mm});
            skLineSegment(sketch, "E180.MirrorCS", {"start": v(36.07, -7.23) * mm, "end": v(35.56, -6.35) * mm});
            skLineSegment(sketch, "E181.MirrorCS", {"start": v(33.66, -7.45) * mm, "end": v(33.02, -6.35) * mm});
            skLineSegment(sketch, "E182.MirrorCS", {"start": v(34.93, -7.45) * mm, "end": v(34.3, -6.35) * mm});
            skLineSegment(sketch, "E183.MirrorCS", {"start": v(-42.16, -7.23) * mm, "end": v(-42.67, -6.35) * mm});
            skLineSegment(sketch, "E184.MirrorCS", {"start": v(-54.86, -6.35) * mm, "end": v(-55.37, -7.23) * mm});
            skLineSegment(sketch, "E185.MirrorCS", {"start": v(29.21, -6.35) * mm, "end": v(28.58, -7.45) * mm});
            skLineSegment(sketch, "E186.MirrorCS", {"start": v(27.94, -6.35) * mm, "end": v(27.3, -7.45) * mm});
            skLineSegment(sketch, "E187.MirrorCS", {"start": v(-39.12, -7.23) * mm, "end": v(-39.62, -6.35) * mm});
            skLineSegment(sketch, "E188.MirrorCS", {"start": v(-11.43, -6.35) * mm, "end": v(-12.07, -7.45) * mm});
            skLineSegment(sketch, "E189.MirrorCS", {"start": v(33.53, -6.35) * mm, "end": v(33.02, -7.23) * mm});
            skLineSegment(sketch, "E190.MirrorCS", {"start": v(-13.97, -6.35) * mm, "end": v(-14.6, -7.45) * mm});
            skLineSegment(sketch, "E191.MirrorCS", {"start": v(47.24, -7.23) * mm, "end": v(46.74, -6.35) * mm});
            skLineSegment(sketch, "E192.MirrorCS", {"start": v(51.3, -7.23) * mm, "end": v(50.8, -6.35) * mm});
            skLineSegment(sketch, "E193.MirrorCS", {"start": v(-19.69, -7.45) * mm, "end": v(-20.32, -6.35) * mm});
            skLineSegment(sketch, "E194.MirrorCS", {"start": v(61.47, -7.23) * mm, "end": v(60.96, -6.35) * mm});
            skLineSegment(sketch, "E195.MirrorCS", {"start": v(32.51, -6.35) * mm, "end": v(32, -7.23) * mm});
            skLineSegment(sketch, "E196.MirrorCS", {"start": v(-61.98, -6.35) * mm, "end": v(-62.48, -7.23) * mm});
            skLineSegment(sketch, "E197.MirrorCS", {"start": v(26.67, -6.35) * mm, "end": v(26.04, -7.45) * mm});
            skLineSegment(sketch, "E198.MirrorCS", {"start": v(-33.53, -6.35) * mm, "end": v(-34.04, -7.23) * mm});
            skLineSegment(sketch, "E199.MirrorCS", {"start": v(46.23, -7.23) * mm, "end": v(45.72, -6.35) * mm});
            skLineSegment(sketch, "E200.MirrorCS", {"start": v(-33.02, -6.35) * mm, "end": v(-33.66, -7.45) * mm});
            skLineSegment(sketch, "E201.MirrorCS", {"start": v(49.78, -6.35) * mm, "end": v(49.28, -7.23) * mm});
            skLineSegment(sketch, "E202.MirrorCS", {"start": v(-9.53, -7.45) * mm, "end": v(-10.16, -6.35) * mm});
            skLineSegment(sketch, "E203.MirrorCS", {"start": v(-41.66, -6.35) * mm, "end": v(-42.16, -7.23) * mm});
            skLineSegment(sketch, "E204.MirrorCS", {"start": v(-59.94, -6.35) * mm, "end": v(-60.45, -7.23) * mm});
            skLineSegment(sketch, "E205.MirrorCS", {"start": v(-42.67, -6.35) * mm, "end": v(-43.18, -7.23) * mm});
            skLineSegment(sketch, "E206.MirrorCS", {"start": v(58.93, -6.35) * mm, "end": v(58.42, -7.23) * mm});
            skLineSegment(sketch, "E207.MirrorCS", {"start": v(56.39, -7.23) * mm, "end": v(55.88, -6.35) * mm});
            skLineSegment(sketch, "E208.MirrorCS", {"start": v(48.77, -6.35) * mm, "end": v(48.26, -7.23) * mm});
            skLineSegment(sketch, "E209.MirrorCS", {"start": v(-63.5, -7.23) * mm, "end": v(-64, -6.35) * mm});
            skLineSegment(sketch, "E210.MirrorCS", {"start": v(-32, -7.23) * mm, "end": v(-32.51, -6.35) * mm});
            skLineSegment(sketch, "E211.MirrorCS", {"start": v(-53.34, -7.23) * mm, "end": v(-53.85, -6.35) * mm});
            skLineSegment(sketch, "E212.MirrorCS", {"start": v(24.13, -6.35) * mm, "end": v(23.5, -7.45) * mm});
            skLineSegment(sketch, "E213.MirrorCS", {"start": v(-53.85, -6.35) * mm, "end": v(-54.36, -7.23) * mm});
            skLineSegment(sketch, "E214.MirrorCS", {"start": v(26.04, -7.45) * mm, "end": v(25.4, -6.35) * mm});
            skLineSegment(sketch, "E215.MirrorCS", {"start": v(59.94, -6.35) * mm, "end": v(59.44, -7.23) * mm});
            skLineSegment(sketch, "E216.MirrorCS", {"start": v(-26.04, -7.45) * mm, "end": v(-26.67, -6.35) * mm});
            skLineSegment(sketch, "E217.MirrorCS", {"start": v(-36.07, -7.23) * mm, "end": v(-36.58, -6.35) * mm});
            skLineSegment(sketch, "E218.MirrorCS", {"start": v(-34.3, -6.35) * mm, "end": v(-34.93, -7.45) * mm});
            skLineSegment(sketch, "E219.MirrorCS", {"start": v(43.18, -7.23) * mm, "end": v(42.67, -6.35) * mm});
            skLineSegment(sketch, "E220.MirrorCS", {"start": v(-63, -6.35) * mm, "end": v(-63.5, -7.23) * mm});
            skLineSegment(sketch, "E221.MirrorCS", {"start": v(55.88, -6.35) * mm, "end": v(55.37, -7.23) * mm});
            skLineSegment(sketch, "E222.MirrorCS", {"start": v(41.15, -7.23) * mm, "end": v(40.64, -6.35) * mm});
            skLineSegment(sketch, "E223.MirrorCS", {"start": v(-46.74, -6.35) * mm, "end": v(-47.24, -7.23) * mm});
            skLineSegment(sketch, "E224.MirrorCS", {"start": v(-15.88, -7.45) * mm, "end": v(-16.51, -6.35) * mm});
            skLineSegment(sketch, "E225.MirrorCS", {"start": v(-31.12, -7.45) * mm, "end": v(-31.75, -6.35) * mm});
            skLineSegment(sketch, "E226.MirrorCS", {"start": v(48.26, -7.23) * mm, "end": v(47.75, -6.35) * mm});
            skLineSegment(sketch, "E227.MirrorCS", {"start": v(-61.47, -7.23) * mm, "end": v(-61.98, -6.35) * mm});
            skLineSegment(sketch, "E228.MirrorCS", {"start": v(-33.02, -7.23) * mm, "end": v(-33.53, -6.35) * mm});
            skLineSegment(sketch, "E229.MirrorCS", {"start": v(-35.56, -6.35) * mm, "end": v(-36.2, -7.45) * mm});
            skLineSegment(sketch, "E230.MirrorCS", {"start": v(25.4, -6.35) * mm, "end": v(24.77, -7.45) * mm});
            skLineSegment(sketch, "E231.MirrorCS", {"start": v(31.5, -6.35) * mm, "end": v(30.99, -7.23) * mm});
            skLineSegment(sketch, "E232.MirrorCS", {"start": v(30.48, -6.35) * mm, "end": v(29.85, -7.45) * mm});
            skLineSegment(sketch, "E233.MirrorCS", {"start": v(19.05, -6.35) * mm, "end": v(18.42, -7.45) * mm});
            skLineSegment(sketch, "E234.MirrorCS", {"start": v(-25.4, -6.35) * mm, "end": v(-26.04, -7.45) * mm});
            skLineSegment(sketch, "E235.MirrorCS", {"start": v(-35.05, -7.23) * mm, "end": v(-35.56, -6.35) * mm});
            skLineSegment(sketch, "E236.MirrorCS", {"start": v(-14.6, -7.45) * mm, "end": v(-15.24, -6.35) * mm});
            skLineSegment(sketch, "E237.MirrorCS", {"start": v(-46.23, -7.23) * mm, "end": v(-46.74, -6.35) * mm});
            skLineSegment(sketch, "E238.MirrorCS", {"start": v(63.5, -7.23) * mm, "end": v(63, -6.35) * mm});
            skLineSegment(sketch, "E239.MirrorCS", {"start": v(45.21, -7.23) * mm, "end": v(44.7, -6.35) * mm});
            skLineSegment(sketch, "E240.MirrorCS", {"start": v(49.28, -7.23) * mm, "end": v(48.77, -6.35) * mm});
            skLineSegment(sketch, "E241.MirrorCS", {"start": v(53.34, -7.23) * mm, "end": v(52.83, -6.35) * mm});
            skLineSegment(sketch, "E242.MirrorCS", {"start": v(50.8, -6.35) * mm, "end": v(50.3, -7.23) * mm});
            skLineSegment(sketch, "E243.MirrorCS", {"start": v(44.2, -7.23) * mm, "end": v(43.69, -6.35) * mm});
            skLineSegment(sketch, "E244.MirrorCS", {"start": v(59.44, -7.23) * mm, "end": v(58.93, -6.35) * mm});
            skLineSegment(sketch, "E245.MirrorCS", {"start": v(-5.08, -6.35) * mm, "end": v(-5.72, -7.45) * mm});
            skLineSegment(sketch, "E246.MirrorCS", {"start": v(-43.69, -6.35) * mm, "end": v(-44.2, -7.23) * mm});
            skLineSegment(sketch, "E247.MirrorCS", {"start": v(47.75, -6.35) * mm, "end": v(47.24, -7.23) * mm});
            skLineSegment(sketch, "E248.MirrorCS", {"start": v(64, -6.35) * mm, "end": v(63.5, -7.23) * mm});
            skLineSegment(sketch, "E249.MirrorCS", {"start": v(-31.5, -6.35) * mm, "end": v(-32, -7.23) * mm});
            skLineSegment(sketch, "E250.MirrorCS", {"start": v(-6.35, -6.35) * mm, "end": v(-6.99, -7.45) * mm});
            skLineSegment(sketch, "E251.MirrorCS", {"start": v(-8.9, -6.35) * mm, "end": v(-9.53, -7.45) * mm});
            skLineSegment(sketch, "E252.MirrorCS", {"start": v(64.52, -7.48) * mm, "end": v(64, -6.6) * mm});
            skLineSegment(sketch, "E253.MirrorCS", {"start": v(-50.3, -7.23) * mm, "end": v(-50.8, -6.35) * mm});
            skLineSegment(sketch, "E254.MirrorCS", {"start": v(-5.72, -7.45) * mm, "end": v(-6.35, -6.35) * mm});
            skLineSegment(sketch, "E255.MirrorCS", {"start": v(-64, -6.1) * mm, "end": v(-64.52, -6.98) * mm});
            skLineSegment(sketch, "E256.MirrorCS", {"start": v(-64.52, -6.98) * mm, "end": v(-65.02, -6.1) * mm});
            skLineSegment(sketch, "E257.MirrorCS", {"start": v(56.9, -6.35) * mm, "end": v(56.39, -7.23) * mm});
            skLineSegment(sketch, "E258.MirrorCS", {"start": v(29.85, -7.45) * mm, "end": v(29.21, -6.35) * mm});
            skLineSegment(sketch, "E259.MirrorCS", {"start": v(-6.99, -7.45) * mm, "end": v(-7.62, -6.35) * mm});
            skLineSegment(sketch, "E260.MirrorCS", {"start": v(-51.3, -7.23) * mm, "end": v(-51.82, -6.35) * mm});
            skLineSegment(sketch, "E261.MirrorCS", {"start": v(-7.62, -6.35) * mm, "end": v(-8.26, -7.45) * mm});
            skLineSegment(sketch, "E262.MirrorCS", {"start": v(20.96, -7.45) * mm, "end": v(20.32, -6.35) * mm});
            skLineSegment(sketch, "E263.MirrorCS", {"start": v(-32.51, -6.35) * mm, "end": v(-33.02, -7.23) * mm});
            skLineSegment(sketch, "E264.MirrorCS", {"start": v(10.8, -7.45) * mm, "end": v(10.16, -6.35) * mm});
            skLineSegment(sketch, "E265.MirrorCS", {"start": v(-43.18, -7.23) * mm, "end": v(-43.69, -6.35) * mm});
            skLineSegment(sketch, "E266.MirrorCS", {"start": v(33.02, -7.23) * mm, "end": v(32.51, -6.35) * mm});
            skLineSegment(sketch, "E267.MirrorCS", {"start": v(57.4, -7.23) * mm, "end": v(56.9, -6.35) * mm});
            skLineSegment(sketch, "E268.MirrorCS", {"start": v(65.02, -6.35) * mm, "end": v(65.02, -6.6) * mm});
            skLineSegment(sketch, "E269.MirrorCS", {"start": v(-65.02, -6.35) * mm, "end": v(65.02, -6.35) * mm});
            skLineSegment(sketch, "E270.MirrorCS", {"start": v(-65.02, -6.35) * mm, "end": v(-65.02, -6.1) * mm});
            skLineSegment(sketch, "E271.MirrorCS", {"start": v(65.02, -6.6) * mm, "end": v(64.52, -7.48) * mm});
            skSolve(sketch);
        }
        {
            var Q0;
            Q0=qSketchRegion(id+"F2",true);
            extrude(context, id + "F3", {"entities" : qUnion([Q0]), "operationType" : NewBodyOperationType.REMOVE, "endBound" : BoundingType.SYMMETRIC, "oppositeDirection" : true, "depth" : 25.4 * mm, "offsetDistance" : 25.4 * mm});
        }
        {
            var Q0;
            Q0=makeQuery(id+"F1.opExtrude","SWEPT_EDGE",EDGE,{"disambiguationData":[OSD([sQuery(id+"F0.wireOp",EDGE,"E0.top"),sQuery(id+"F0.wireOp",EDGE,"E3.trimOffspring")])]});
            var Q1;
            Q1=makeQuery(id+"F1.opExtrude","SWEPT_EDGE",EDGE,{"disambiguationData":[OSD([sQuery(id+"F0.wireOp",EDGE,"E0.top"),sQuery(id+"F0.wireOp",EDGE,"E2.trimOffspring")])]});
            var Q2;
            Q2=makeQuery(id+"F1.opExtrude","SWEPT_EDGE",EDGE,{"disambiguationData":[OSD([sQuery(id+"F0.wireOp",EDGE,"E0.bottom"),sQuery(id+"F0.wireOp",EDGE,"E0.left")])]});
            var Q3;
            Q3=makeQuery(id+"F1.opExtrude","SWEPT_EDGE",EDGE,{"disambiguationData":[OSD([sQuery(id+"F0.wireOp",EDGE,"E0.bottom"),sQuery(id+"F0.wireOp",EDGE,"E0.right")])]});
            fillet(context, id + "F4", {"entities" : qUnion([Q0, Q1, Q2, Q3]), "radius" : 5.08 * mm, "tangentPropagation" : true, "allowEdgeOverflow" : false});
        }
        {
            var Q0;
            Q0=makeQuery(id+"F1.opExtrude","CAP_EDGE",EDGE,{"disambiguationData":[OSD([sQuery(id+"F0.wireOp",EDGE,"E0.top")])],"isStart":false});
            var Q1;
            Q1=makeQuery(id+"F1.opExtrude","CAP_EDGE",EDGE,{"disambiguationData":[OSD([sQuery(id+"F0.wireOp",EDGE,"E0.top")])],"isStart":true});
            var Q2;
            Q2=makeQuery(id+"F1.opExtrude","CAP_EDGE",EDGE,{"disambiguationData":[OSD([sQuery(id+"F0.wireOp",EDGE,"E0.bottom")])],"isStart":false});
            var Q3;
            Q3=makeQuery(id+"F1.opExtrude","CAP_EDGE",EDGE,{"disambiguationData":[OSD([sQuery(id+"F0.wireOp",EDGE,"E0.bottom")])],"isStart":true});
            fillet(context, id + "F5", {"entities" : qUnion([Q0, Q1, Q2, Q3]), "radius" : 0.5 * mm, "tangentPropagation" : true, "allowEdgeOverflow" : false});
        }
    });
